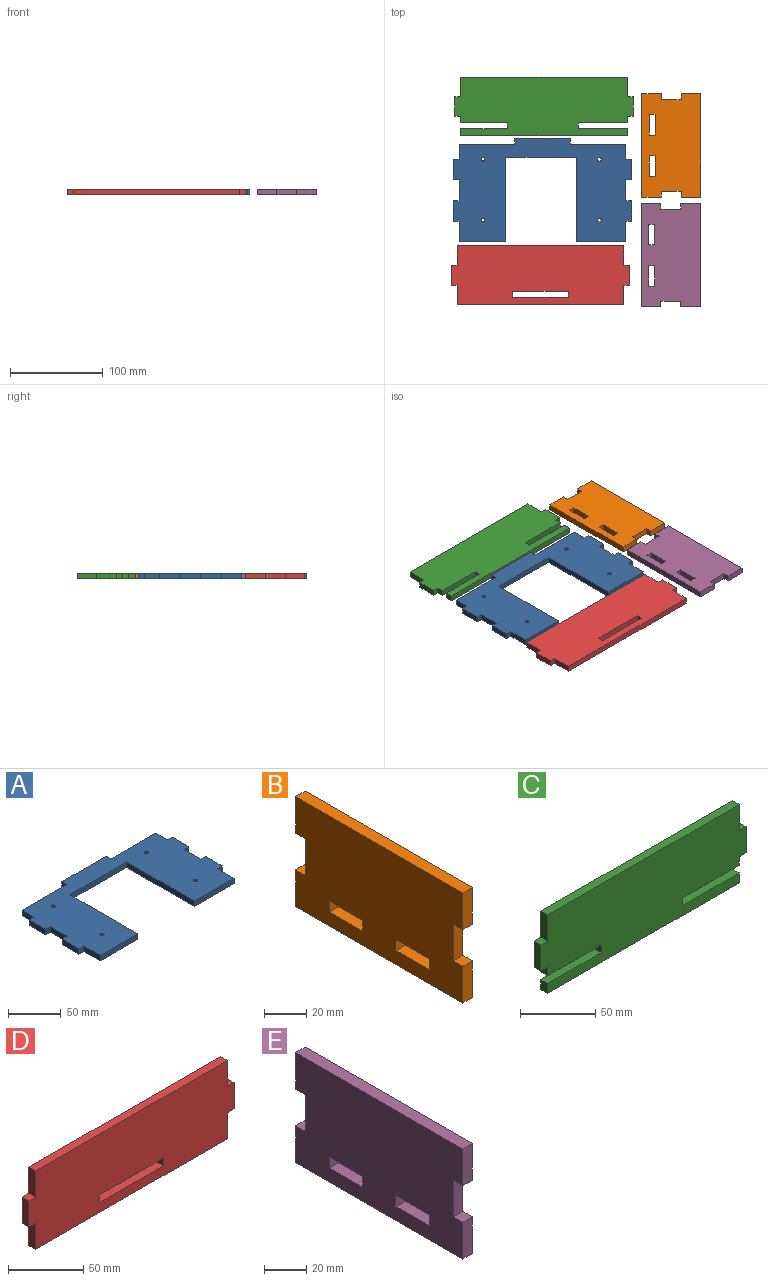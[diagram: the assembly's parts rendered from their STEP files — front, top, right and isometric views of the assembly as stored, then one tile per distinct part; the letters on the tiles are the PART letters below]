
ASSEMBLY  parts=5 mates=4
PART A: 34 faces, bbox 192.2x111.5x6.4 mm
  f0: plane 192.23x111.52mm, normal (0,0,1), area 12826.5mm2, adj f2,f3,f4,f5,f6,f7,f8,f9
  f1: plane 192.23x111.52mm, normal (0,0,-1), area 12826.5mm2, adj f2,f3,f4,f5,f6,f7,f8,f9
  f2: plane 53.06x6.35mm, normal (0,-1,0), area 337mm2, adj f0,f1,f10,f25
  f3: plane 22.3x6.35mm, normal (1,0,0), area 141.6mm2, adj f0,f1,f26,f28
  f4: plane 22.3x6.35mm, normal (1,0,0), area 141.6mm2, adj f0,f1,f24,f29
  f5: plane 22.3x6.35mm, normal (-1,0,0), area 141.6mm2, adj f0,f1,f17,f20
  f6: plane 22.3x6.35mm, normal (-1,0,0), area 141.6mm2, adj f0,f1,f19,f22
  f7: plane 59.84x6.35mm, normal (0,1,0), area 380mm2, adj f0,f1,f13,f15
  f8: plane 91.2x6.35mm, normal (1,0,0), area 579.1mm2, adj f0,f1,f9,f11
  f9: plane 76.2x6.35mm, normal (0,-1,0), area 483.9mm2, adj f0,f1,f8,f10
  f10: plane 91.2x6.35mm, normal (-1,0,0), area 579.1mm2, adj f0,f1,f2,f9
  f11: plane 50.27x6.35mm, normal (0,-1,0), area 319.2mm2, adj f0,f1,f8,f21
  f12: plane 59.84x6.35mm, normal (0,1,0), area 380mm2, adj f0,f1,f13,f23
  f13: plane 6.35x6.35mm, normal (1,0,0), area 40.3mm2, adj f0,f1,f7,f12
  f14: plane 59.84x6.35mm, normal (0,1,0), area 380mm2, adj f0,f1,f15,f16
  f15: plane 6.35x6.35mm, normal (-1,0,0), area 40.3mm2, adj f0,f1,f7,f14
  f16: plane 15.95x6.35mm, normal (-1,0,0), area 101.3mm2, adj f0,f1,f14,f17
  f17: plane 6.35x6.35mm, normal (0,1,0), area 40.3mm2, adj f0,f1,f5,f16
  f18: plane 22.3x6.35mm, normal (-1,0,0), area 141.6mm2, adj f0,f1,f19,f20
  f19: plane 6.35x6.35mm, normal (0,1,0), area 40.3mm2, adj f0,f1,f6,f18
  f20: plane 6.35x6.35mm, normal (0,-1,0), area 40.3mm2, adj f0,f1,f5,f18
  f21: plane 22.3x6.35mm, normal (-1,0,0), area 141.6mm2, adj f0,f1,f11,f22
  f22: plane 6.35x6.35mm, normal (0,-1,0), area 40.3mm2, adj f0,f1,f6,f21
  f23: plane 15.95x6.35mm, normal (1,0,0), area 101.3mm2, adj f0,f1,f12,f24
  f24: plane 6.35x6.35mm, normal (0,1,0), area 40.3mm2, adj f0,f1,f4,f23
  f25: plane 22.3x6.35mm, normal (1,0,0), area 141.6mm2, adj f0,f1,f2,f26
  f26: plane 6.35x6.35mm, normal (0,-1,0), area 40.3mm2, adj f0,f1,f3,f25
  f27: plane 22.3x6.35mm, normal (1,0,0), area 141.6mm2, adj f0,f1,f28,f29
  f28: plane 6.35x6.35mm, normal (0,1,0), area 40.3mm2, adj f0,f1,f3,f27
  f29: plane 6.35x6.35mm, normal (0,-1,0), area 40.3mm2, adj f0,f1,f4,f27
  f30: cylinder r=2.03mm len=6.35mm, axis (0,0,1), area 81.1mm2, adj f0,f1
  f31: cylinder r=2.03mm len=6.35mm, axis (0,0,1), area 81.1mm2, adj f0,f1
  f32: cylinder r=2.03mm len=6.35mm, axis (0,0,1), area 81.1mm2, adj f0,f1
  f33: cylinder r=2.03mm len=6.35mm, axis (0,0,1), area 81.1mm2, adj f0,f1
PART B: 22 faces, bbox 6.4x111.5x63.5 mm
  f0: plane 111.52x63.5mm, normal (-1,0,0), area 6529.4mm2, adj f2,f3,f4,f5,f6,f7,f8,f9
  f1: plane 111.52x63.5mm, normal (1,0,0), area 6529.4mm2, adj f2,f3,f4,f5,f6,f7,f8,f9
  f2: plane 21.17x6.35mm, normal (0,1,0), area 134.4mm2, adj f0,f1,f6,f11
  f3: plane 21.17x6.35mm, normal (0,-1,0), area 134.4mm2, adj f0,f1,f7,f10
  f4: plane 21.17x6.35mm, normal (0,1,0), area 134.4mm2, adj f0,f1,f7,f12
  f5: plane 21.17x6.35mm, normal (0,-1,0), area 134.4mm2, adj f0,f1,f6,f9
  f6: plane 111.52x6.35mm, normal (0,0,1), area 708.1mm2, adj f0,f1,f2,f5
  f7: plane 111.52x6.35mm, normal (0,0,-1), area 708.1mm2, adj f0,f1,f3,f4
  f8: plane 21.17x6.35mm, normal (0,-1,0), area 134.4mm2, adj f0,f1,f9,f10
  f9: plane 6.35x6.35mm, normal (0,0,-1), area 40.3mm2, adj f0,f1,f5,f8
  f10: plane 6.35x6.35mm, normal (0,0,1), area 40.3mm2, adj f0,f1,f3,f8
  f11: plane 6.35x6.35mm, normal (0,0,-1), area 40.3mm2, adj f0,f1,f2,f13
  f12: plane 6.35x6.35mm, normal (0,0,1), area 40.3mm2, adj f0,f1,f4,f13
  f13: plane 21.17x6.35mm, normal (0,1,0), area 134.4mm2, adj f0,f1,f11,f12
  f14: plane 6.35x6.35mm, normal (0,1,0), area 40.3mm2, adj f0,f1,f15,f16
  f15: plane 22.3x6.35mm, normal (0,0,-1), area 141.6mm2, adj f0,f1,f14,f17
  f16: plane 22.3x6.35mm, normal (0,0,1), area 141.6mm2, adj f0,f1,f14,f17
  f17: plane 6.35x6.35mm, normal (0,-1,0), area 40.3mm2, adj f0,f1,f15,f16
  f18: plane 6.35x6.35mm, normal (0,1,0), area 40.3mm2, adj f0,f1,f19,f20
  f19: plane 22.3x6.35mm, normal (0,0,-1), area 141.6mm2, adj f0,f1,f18,f21
  f20: plane 22.3x6.35mm, normal (0,0,1), area 141.6mm2, adj f0,f1,f18,f21
  f21: plane 6.35x6.35mm, normal (0,-1,0), area 40.3mm2, adj f0,f1,f19,f20
PART C: 22 faces, bbox 192.2x6.4x63.5 mm
  f0: plane 7.95x6.35mm, normal (1,0,0), area 50.5mm2, adj f4,f5,f7,f21
  f1: plane 7.95x6.35mm, normal (-1,0,0), area 50.5mm2, adj f4,f5,f7,f17
  f2: plane 21.17x6.35mm, normal (-1,0,0), area 134.4mm2, adj f5,f7,f13,f15
  f3: plane 179.53x6.35mm, normal (0,0,1), area 1140mm2, adj f5,f7,f10,f12
  f4: plane 179.53x6.35mm, normal (0,0,-1), area 1140mm2, adj f0,f1,f5,f7
  f5: plane 192.23x63.5mm, normal (0,-1,0), area 11013mm2, adj f0,f1,f2,f3,f4,f6,f8,f9
  f6: plane 21.17x6.35mm, normal (1,0,0), area 134.4mm2, adj f5,f7,f9,f11
  f7: plane 192.23x63.5mm, normal (0,1,0), area 11013mm2, adj f0,f1,f2,f3,f4,f6,f8,f9
  f8: plane 6.87x6.35mm, normal (1,0,0), area 43.6mm2, adj f5,f7,f9,f20
  f9: plane 6.35x6.35mm, normal (0,0,-1), area 40.3mm2, adj f5,f6,f7,f8
  f10: plane 21.17x6.35mm, normal (1,0,0), area 134.4mm2, adj f3,f5,f7,f11
  f11: plane 6.35x6.35mm, normal (0,0,1), area 40.3mm2, adj f5,f6,f7,f10
  f12: plane 21.17x6.35mm, normal (-1,0,0), area 134.4mm2, adj f3,f5,f7,f13
  f13: plane 6.35x6.35mm, normal (0,0,1), area 40.3mm2, adj f2,f5,f7,f12
  f14: plane 6.87x6.35mm, normal (-1,0,0), area 43.6mm2, adj f5,f7,f15,f16
  f15: plane 6.35x6.35mm, normal (0,0,-1), area 40.3mm2, adj f2,f5,f7,f14
  f16: plane 50.27x6.35mm, normal (0,0,-1), area 319.2mm2, adj f5,f7,f14,f18
  f17: plane 50.27x6.35mm, normal (0,0,1), area 319.2mm2, adj f1,f5,f7,f18
  f18: plane 6.35x6.35mm, normal (-1,0,0), area 40.3mm2, adj f5,f7,f16,f17
  f19: plane 6.35x6.35mm, normal (1,0,0), area 40.3mm2, adj f5,f7,f20,f21
  f20: plane 53.06x6.35mm, normal (0,0,-1), area 337mm2, adj f5,f7,f8,f19
  f21: plane 53.06x6.35mm, normal (0,0,1), area 337mm2, adj f0,f5,f7,f19
PART D: 18 faces, bbox 192.2x6.4x63.5 mm
  f0: plane 192.23x63.5mm, normal (0,-1,0), area 11289.1mm2, adj f1,f3,f4,f5,f6,f7,f8,f9
  f1: plane 21.17x6.35mm, normal (1,0,0), area 134.4mm2, adj f0,f2,f11,f13
  f2: plane 192.23x63.5mm, normal (0,1,0), area 11289.1mm2, adj f1,f3,f4,f5,f6,f7,f8,f9
  f3: plane 21.17x6.35mm, normal (-1,0,0), area 134.4mm2, adj f0,f2,f7,f9
  f4: plane 179.53x6.35mm, normal (0,0,1), area 1140mm2, adj f0,f2,f8,f10
  f5: plane 179.53x6.35mm, normal (0,0,-1), area 1140mm2, adj f0,f2,f6,f12
  f6: plane 21.17x6.35mm, normal (-1,0,0), area 134.4mm2, adj f0,f2,f5,f7
  f7: plane 6.35x6.35mm, normal (0,0,-1), area 40.3mm2, adj f0,f2,f3,f6
  f8: plane 21.17x6.35mm, normal (-1,0,0), area 134.4mm2, adj f0,f2,f4,f9
  f9: plane 6.35x6.35mm, normal (0,0,1), area 40.3mm2, adj f0,f2,f3,f8
  f10: plane 21.17x6.35mm, normal (1,0,0), area 134.4mm2, adj f0,f2,f4,f11
  f11: plane 6.35x6.35mm, normal (0,0,1), area 40.3mm2, adj f0,f1,f2,f10
  f12: plane 21.17x6.35mm, normal (1,0,0), area 134.4mm2, adj f0,f2,f5,f13
  f13: plane 6.35x6.35mm, normal (0,0,-1), area 40.3mm2, adj f0,f1,f2,f12
  f14: plane 6.35x6.35mm, normal (1,0,0), area 40.3mm2, adj f0,f2,f16,f17
  f15: plane 6.35x6.35mm, normal (-1,0,0), area 40.3mm2, adj f0,f2,f16,f17
  f16: plane 59.84x6.35mm, normal (0,0,1), area 380mm2, adj f0,f2,f14,f15
  f17: plane 59.84x6.35mm, normal (0,0,-1), area 380mm2, adj f0,f2,f14,f15
PART E: 22 faces, bbox 6.4x111.5x63.5 mm
  f0: plane 21.17x6.35mm, normal (0,1,0), area 134.4mm2, adj f2,f3,f7,f12
  f1: plane 21.17x6.35mm, normal (0,-1,0), area 134.4mm2, adj f2,f3,f7,f9
  f2: plane 111.52x63.5mm, normal (1,0,0), area 6529.4mm2, adj f0,f1,f4,f5,f6,f7,f8,f9
  f3: plane 111.52x63.5mm, normal (-1,0,0), area 6529.4mm2, adj f0,f1,f4,f5,f6,f7,f8,f9
  f4: plane 21.17x6.35mm, normal (0,1,0), area 134.4mm2, adj f2,f3,f6,f11
  f5: plane 21.17x6.35mm, normal (0,-1,0), area 134.4mm2, adj f2,f3,f6,f8
  f6: plane 111.52x6.35mm, normal (0,0,1), area 708.1mm2, adj f2,f3,f4,f5
  f7: plane 111.52x6.35mm, normal (0,0,-1), area 708.1mm2, adj f0,f1,f2,f3
  f8: plane 6.35x6.35mm, normal (0,0,-1), area 40.3mm2, adj f2,f3,f5,f10
  f9: plane 6.35x6.35mm, normal (0,0,1), area 40.3mm2, adj f1,f2,f3,f10
  f10: plane 21.17x6.35mm, normal (0,-1,0), area 134.4mm2, adj f2,f3,f8,f9
  f11: plane 6.35x6.35mm, normal (0,0,-1), area 40.3mm2, adj f2,f3,f4,f13
  f12: plane 6.35x6.35mm, normal (0,0,1), area 40.3mm2, adj f0,f2,f3,f13
  f13: plane 21.17x6.35mm, normal (0,1,0), area 134.4mm2, adj f2,f3,f11,f12
  f14: plane 6.35x6.35mm, normal (0,-1,0), area 40.3mm2, adj f2,f3,f15,f16
  f15: plane 22.3x6.35mm, normal (0,0,-1), area 141.6mm2, adj f2,f3,f14,f17
  f16: plane 22.3x6.35mm, normal (0,0,1), area 141.6mm2, adj f2,f3,f14,f17
  f17: plane 6.35x6.35mm, normal (0,1,0), area 40.3mm2, adj f2,f3,f15,f16
  f18: plane 6.35x6.35mm, normal (0,-1,0), area 40.3mm2, adj f2,f3,f19,f20
  f19: plane 22.3x6.35mm, normal (0,0,-1), area 141.6mm2, adj f2,f3,f18,f21
  f20: plane 22.3x6.35mm, normal (0,0,1), area 141.6mm2, adj f2,f3,f18,f21
  f21: plane 6.35x6.35mm, normal (0,1,0), area 40.3mm2, adj f2,f3,f19,f20
PLACE A t=(8.61,-32.03,17)mm fixed
PLACE B rot(axis=(0,1,0),90deg) t=(117.03,16.15,122.46)mm
PLACE C rot(axis=(-1,0,0),90deg) t=(10.31,25.83,-24.94)mm
PLACE D rot(axis=(-1,0,0),90deg) t=(6.47,-155.84,80.23)mm
PLACE E rot(axis=(0,1,0),90deg) t=(116.41,-102.08,-63.42)mm
MATE planar E.f2 <-> A.f32  axis (0,0,-1) through (149.06,-102.57,24.95)mm
MATE planar D.f2 <-> A.f30  axis (0,0,-1) through (7.87,-123.39,24.95)mm
MATE planar C.f7 <-> A.f30  axis (0,0,-1) through (11.64,58.81,24.95)mm
MATE planar B.f1 <-> A.f33  axis (0,0,-1) through (149.68,15.67,24.95)mm
